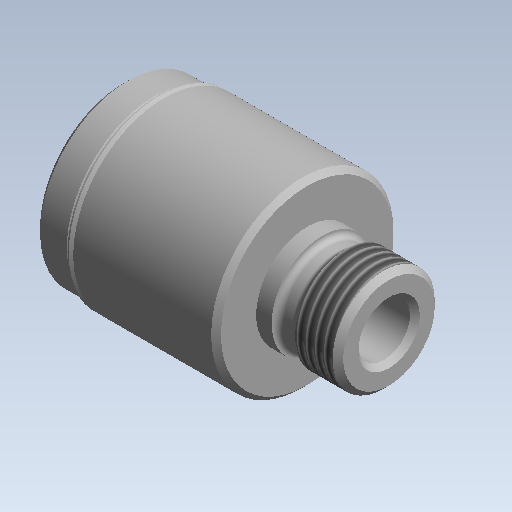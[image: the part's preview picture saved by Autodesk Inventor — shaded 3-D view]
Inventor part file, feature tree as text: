
AUTODESK INVENTOR PART (.ipt)
format: ipt  version: 2020 (Build 240168000, 168)  size: 268,288 bytes
history: native  units: mm (DEFAULTED — no unit token found)
features: other x119, sketch x5, revolve x4, thread x2, hole x1
ambient origin geometry x8: Origin, YZ Plane, XZ Plane, XY Plane, X Axis, Y Axis, Z Axis, Center Point
bodies: Solid1 (feature_tree)
feature tree (131):
  revolve  "Revolution1"  [1 undecoded]
  thread  "Thread1"  [1 undecoded]
  revolve  "Revolution2"  Angle=360.0deg
  hole  "Hole1"  [1 undecoded]
  revolve  "Revolution3"  [1 undecoded]
  thread  "Thread2"  [1 undecoded]
  revolve  "Revolution4"  [1 undecoded]
  other  "dp1_XY"
  other  "dp1_YZ"
  other  "dp1_ZX"
  other  "dp1_X"
  other  "dp1_Y"
  other  "dp1_Z"
  other  "dp1_Center"
  other  "dp2_XY"
  other  "dp2_YZ"
  other  "dp2_ZX"
  other  "dp2_X"
  other  "dp2_Y"
  other  "dp2_Z"
  other  "dp2_Center"
  other  "hh_XY"
  other  "hh_YZ"
  other  "hh_ZX"
  other  "hh_X"
  other  "hh_Y"
  other  "hh_Z"
  other  "hh_Center"
  other  "port_XY"
  other  "port_YZ"
  other  "port_ZX"
  other  "port_X"
  other  "port_Y"
  other  "port_Z"
  other  "port_Center"
  other  "rod_guide_XY"
  other  "rod_guide_YZ"
  other  "rod_guide_ZX"
  other  "rod_guide_X"
  other  "rod_guide_Y"
  other  "rod_guide_Z"
  other  "rod_guide_Center"
  other  "s1_XY"
  other  "s1_YZ"
  other  "s1_ZX"
  other  "s1_X"
  other  "s1_Y"
  other  "s1_Z"
  other  "s1_Center"
  other  "s2_XY"
  other  "s2_YZ"
  other  "s2_ZX"
  other  "s2_X"
  other  "s2_Y"
  other  "s2_Z"
  other  "s2_Center"
  other  "t1_XY"
  other  "t1_YZ"
  other  "t1_ZX"
  other  "t1_X"
  other  "t1_Y"
  other  "t1_Z"
  other  "t1_Center"
  other  "t111_XY"
  other  "t111_YZ"
  other  "t111_ZX"
  other  "t111_X"
  other  "t111_Y"
  other  "t111_Z"
  other  "t111_Center"
  other  "to_foot_bracket_XY"
  other  "to_foot_bracket_YZ"
  other  "to_foot_bracket_ZX"
  other  "to_foot_bracket_X"
  other  "to_foot_bracket_Y"
  other  "to_foot_bracket_Z"
  other  "to_foot_bracket_Center"
  other  "to_nut_XY"
  other  "to_nut_YZ"
  other  "to_nut_ZX"
  other  "to_nut_X"
  other  "to_nut_Y"
  other  "to_nut_Z"
  other  "to_nut_Center"
  other  "to_rod_XY"
  other  "to_rod_YZ"
  other  "to_rod_ZX"
  other  "to_rod_X"
  other  "to_rod_Y"
  other  "to_rod_Z"
  other  "to_rod_Center"
  other  "to_screw_XY"
  other  "to_screw_YZ"
  other  "to_screw_ZX"
  other  "to_screw_X"
  other  "to_screw_Y"
  other  "to_screw_Z"
  other  "to_screw_Center"
  other  "to_trunnion_brackets_XY"
  other  "to_trunnion_brackets_YZ"
  other  "to_trunnion_brackets_ZX"
  other  "to_trunnion_brackets_X"
  other  "to_trunnion_brackets_Y"
  other  "to_trunnion_brackets_Z"
  other  "to_trunnion_brackets_Center"
  other  "to_trunnion_brackets1_XY"
  other  "to_trunnion_brackets1_YZ"
  other  "to_trunnion_brackets1_ZX"
  other  "to_trunnion_brackets1_X"
  other  "to_trunnion_brackets1_Y"
  other  "to_trunnion_brackets1_Z"
  other  "to_trunnion_brackets1_Center"
  other  "to_trunnion_brackets2_XY"
  other  "to_trunnion_brackets2_YZ"
  other  "to_trunnion_brackets2_ZX"
  other  "to_trunnion_brackets2_X"
  other  "to_trunnion_brackets2_Y"
  other  "to_trunnion_brackets2_Z"
  other  "to_trunnion_brackets2_Center"
  other  "to_tube_XY"
  other  "to_tube_YZ"
  other  "to_tube_ZX"
  other  "to_tube_X"
  other  "to_tube_Y"
  other  "to_tube_Z"
  other  "to_tube_Center"
  sketch  "Sketch_2"  dims[d0=360.0deg d1=5.83314mm d2=0.0mm d3=360.0deg]
  sketch  "Sketch_3"  dims[d4=8.0264mm d5=6.0mm d6=9.5504mm d7=2.0mm d8=90.0deg d9=41.275mm d10=0.0mm d11=360.0deg]
  sketch  "Sketch3"  dims[d12=5.71778mm d13=0.0mm d14=360.0deg]
  sketch  "Sketch_40"  dims[d15=0.0mm d16=0.0mm d17=0.0mm d18=0.0mm d19=0.0mm d20=0.0mm]
  sketch  "Sketch_47"
note: 6 required parameter values undecoded (feature->parameter linkage not recoverable at this tier; creation-order binding heuristic only, values carry confidence <= 0.55)